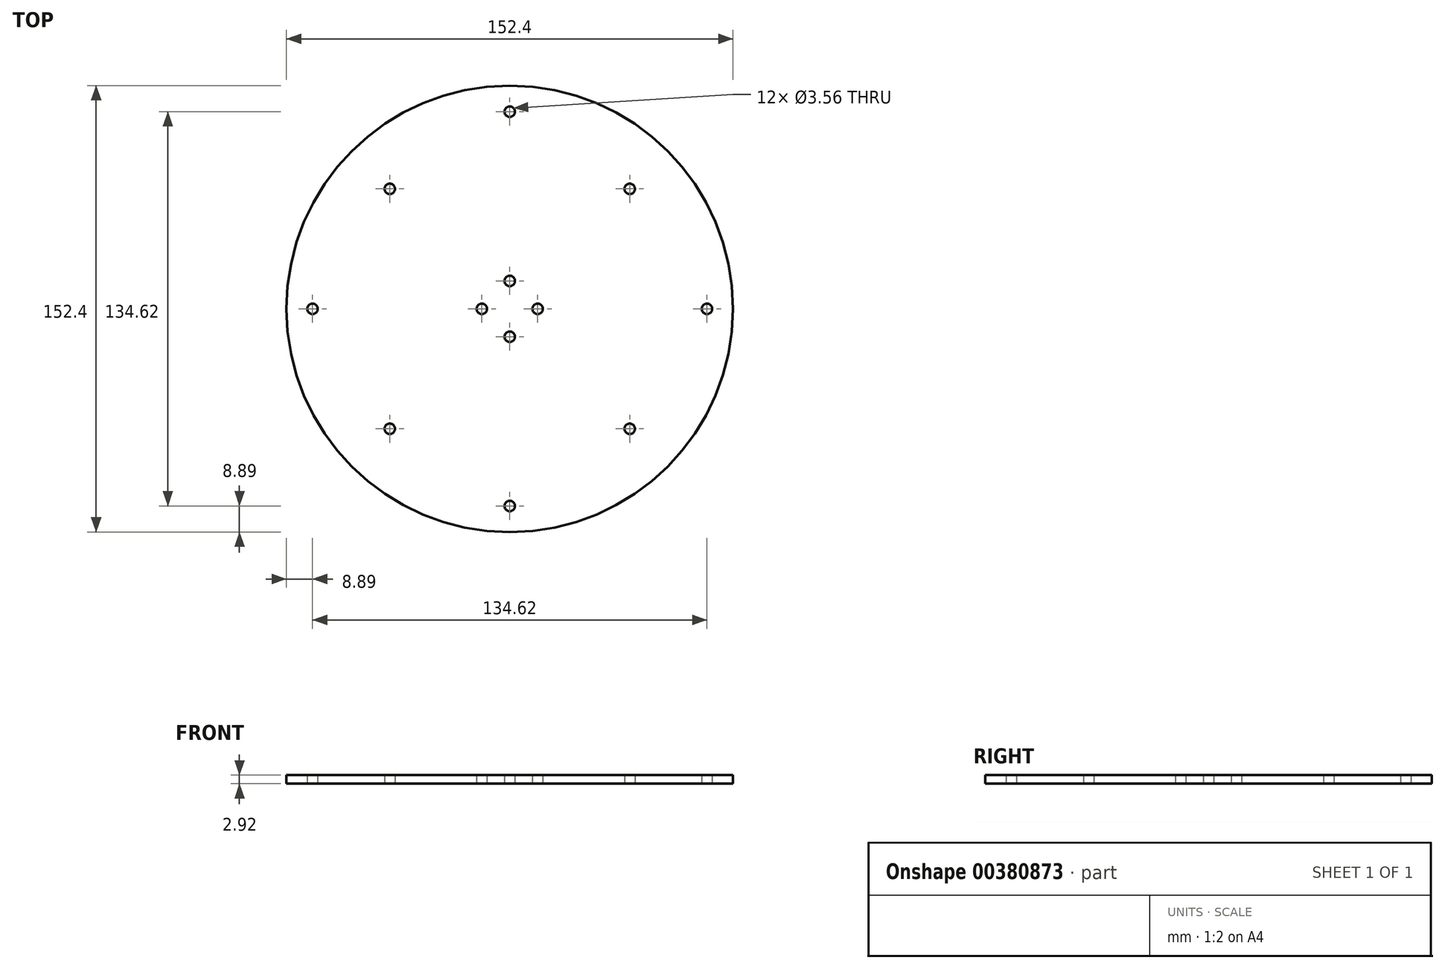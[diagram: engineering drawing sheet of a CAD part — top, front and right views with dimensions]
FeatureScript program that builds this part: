
annotation { "Feature Type Name" : "Feature", "Feature Type Description" : "" }
export const myFeature = defineFeature(function(context is Context, id is Id, definition is map)
    precondition{}
    {
        {
            var Q0;
            Q0=qCreatedBy(makeId("Top.planeOp"),FACE);
            var sketch = newSketch(context, id + "F0", { "sketchPlane" : qUnion([Q0])});
            skCircle(sketch, "E0", {"center": v(76.2, 76.2) * mm, "radius": 76.2 * mm});
            skCircle(sketch, "E1", {"center": v(76.2, 85.73) * mm, "radius": 1.78 * mm});
            skCircle(sketch, "E2.1.0", {"center": v(66.67, 76.2) * mm, "radius": 1.78 * mm});
            skCircle(sketch, "E2.2.0", {"center": v(76.2, 66.67) * mm, "radius": 1.78 * mm});
            skCircle(sketch, "E2.3.0", {"center": v(85.73, 76.2) * mm, "radius": 1.78 * mm});
            skCircle(sketch, "E3", {"center": v(117.15, 117.15) * mm, "radius": 1.78 * mm});
            skCircle(sketch, "E4.1.0", {"center": v(35.25, 117.15) * mm, "radius": 1.78 * mm});
            skCircle(sketch, "E4.2.0", {"center": v(35.25, 35.25) * mm, "radius": 1.78 * mm});
            skCircle(sketch, "E4.3.0", {"center": v(117.15, 35.25) * mm, "radius": 1.78 * mm});
            skCircle(sketch, "E5", {"center": v(76.2, 143.51) * mm, "radius": 1.78 * mm});
            skCircle(sketch, "E6.1.0", {"center": v(8.89, 76.2) * mm, "radius": 1.78 * mm});
            skCircle(sketch, "E6.2.0", {"center": v(76.2, 8.9) * mm, "radius": 1.78 * mm});
            skCircle(sketch, "E6.3.0", {"center": v(143.51, 76.2) * mm, "radius": 1.78 * mm});
            skLineSegment(sketch, "E7", {"start": v(76.2, 76.2) * mm, "end": v(117.3, 117.3) * mm, "construction": true});
            skLineSegment(sketch, "E8", {"start": v(76.2, 76.2) * mm, "end": v(98.29, 76.2) * mm, "construction": true});
            skSolve(sketch);
        }
        {
            var Q0;
            Q0 = qSketchRegion(id + "F0", true);
            extrude(context, id + "F1", {"entities" : qUnion([Q0]), "depth" : 2.92 * mm});
        }
    });
